FCSTD DOCUMENT  (FreeCAD 0.20R26155 (Git))
Label: SWD_pogo
License: All rights reserved
LicenseURL: http://en.wikipedia.org/wiki/All_rights_reserved
objects: Sketcher::SketchObject×2
note: 2 computed .brp shape members not serialized (recipe doc carries the construction recipe); baked Part::Feature solids carry a one-line shape summary decoded from their .brp

FEATURE [Sketcher::SketchObject] Sketch  label="Pads_TH_SMD"
  FullyConstrained = true
  sketch-geometry (15):
    g0: LineSegment StartX=-0.35 StartY=0 StartZ=0 EndX=0.35 EndY=0 EndZ=0
    g1: LineSegment StartX=0.35 StartY=0 StartZ=0 EndX=0.35 EndY=2.2 EndZ=0
    g2: LineSegment StartX=0.35 StartY=2.2 StartZ=0 EndX=-0.35 EndY=2.2 EndZ=0
    g3: LineSegment StartX=-0.35 StartY=2.2 StartZ=0 EndX=-0.35 EndY=0 EndZ=0
    g4: LineSegment StartX=1.85 StartY=-2.2e-15 StartZ=0 EndX=2.55 EndY=-2.2e-15 EndZ=0
    g5: LineSegment StartX=2.55 StartY=-2.2e-15 StartZ=0 EndX=2.55 EndY=2.2 EndZ=0
    g6: LineSegment StartX=2.55 StartY=2.2 StartZ=0 EndX=1.85 EndY=2.2 EndZ=0
    g7: LineSegment StartX=1.85 StartY=2.2 StartZ=0 EndX=1.85 EndY=-2.2e-15 EndZ=0
    g8: LineSegment StartX=-2.55 StartY=2.7e-15 StartZ=0 EndX=-1.85 EndY=2.7e-15 EndZ=0
    g9: LineSegment StartX=-1.85 StartY=2.7e-15 StartZ=0 EndX=-1.85 EndY=2.2 EndZ=0
    g10: LineSegment StartX=-1.85 StartY=2.2 StartZ=0 EndX=-2.55 EndY=2.2 EndZ=0
    g11: LineSegment StartX=-2.55 StartY=2.2 StartZ=0 EndX=-2.55 EndY=2.7e-15 EndZ=0
    g12: LineSegment StartX=-2.55 StartY=2.2 StartZ=0 EndX=2.55 EndY=2.2 EndZ=0
    g13: LineSegment StartX=-2.2 StartY=2.2 StartZ=0 EndX=-2.2 EndY=2.7e-15 EndZ=0
    g14: LineSegment StartX=2.2 StartY=2.2 StartZ=0 EndX=2.2 EndY=-2.2e-15 EndZ=0
  constraints (43):
    c: Coincident(g0,g1)
    c: Coincident(g1,g2)
    c: Coincident(g2,g3)
    c: Coincident(g3,g0)
    c: Horizontal(g0)
    c: Vertical(g1)
    c: Vertical(g3)
    c: Coincident(g4,g5)
    c: Coincident(g5,g6)
    c: Coincident(g6,g7)
    c: Coincident(g7,g4)
    c: Horizontal(g4)
    c: Horizontal(g6)
    c: Vertical(g5)
    c: Vertical(g7)
    c: Coincident(g8,g9)
    c: Coincident(g9,g10)
    c: Coincident(g10,g11)
    c: Coincident(g11,g8)
    c: Horizontal(g8)
    c: Horizontal(g10)
    c: Vertical(g9)
    c: Vertical(g11)
    c: Equal(g2,g6)
    c: Equal(g6,g10)
    c: Equal(g9,g1)
    c: Equal(g1,g5)
    c: Coincident(g12,g10)
    c: Coincident(g12,g5)
    c: Horizontal(g12)
    c: PointOnObject(g1,g12)
    c: DistanceY(g11,g11) = 2.2
    c: Symmetric(g2,g1,g-2)
    c: PointOnObject(g13,g10)
    c: PointOnObject(g13,g8)
    c: PointOnObject(g14,g6)
    c: PointOnObject(g14,g4)
    c: Symmetric(g6,g5,g14)
    c: Symmetric(g10,g9,g13)
    c: DistanceX(g13,g-1) = 2.2
    c: DistanceX(g-1,g14) = 2.2
    c: DistanceX(g8,g8) = 0.7
    c: PointOnObject(g0,g-1)
FEATURE [Sketcher::SketchObject] Sketch001  label="Edge_Cuts_0.15"
  ExternalGeometry = -> [Sketch]
  FullyConstrained = true
  sketch-geometry (21):
    g0: LineSegment StartX=-3.05 StartY=2.7 StartZ=0 EndX=3.05 EndY=2.7 EndZ=0
    g1: LineSegment StartX=3.55 StartY=3.2 StartZ=0 EndX=3.55 EndY=9.2 EndZ=0
    g2: LineSegment StartX=4.05 StartY=9.7 StartZ=0 EndX=6.05 EndY=9.7 EndZ=0
    g3: LineSegment StartX=7.5 StartY=-28.3 StartZ=0 EndX=-4.5 EndY=-28.3 EndZ=0
    g4: ArcOfCircle CenterX=4.05 CenterY=9.2 CenterZ=0 NormalX=0 NormalY=0 NormalZ=1 AngleXU=0 Radius=0.5 StartAngle=1.5708 EndAngle=3.14159
    g5: ArcOfCircle CenterX=6.05 CenterY=9.2 CenterZ=0 NormalX=0 NormalY=0 NormalZ=1 AngleXU=0 Radius=0.5 StartAngle=-9e-16 EndAngle=1.5708
    g6: ArcOfCircle CenterX=-3.05 CenterY=2.2 CenterZ=0 NormalX=0 NormalY=0 NormalZ=1 AngleXU=0 Radius=0.5 StartAngle=1.5708 EndAngle=3.14159
    g7: ArcOfCircle CenterX=3.05 CenterY=3.2 CenterZ=0 NormalX=0 NormalY=0 NormalZ=1 AngleXU=0 Radius=0.5 StartAngle=4.71239 EndAngle=6.28319
    g8: ArcOfCircle CenterX=-4.5 CenterY=-27.8 CenterZ=0 NormalX=0 NormalY=0 NormalZ=1 AngleXU=0 Radius=0.5 StartAngle=3.14159 EndAngle=4.71239
    g9: ArcOfCircle CenterX=7.5 CenterY=-27.8 CenterZ=0 NormalX=0 NormalY=0 NormalZ=1 AngleXU=0 Radius=0.5 StartAngle=4.71239 EndAngle=6.28319
    g10: LineSegment StartX=-5 StartY=-27.8 StartZ=0 EndX=-5 EndY=-16.8 EndZ=0
    g11: LineSegment StartX=-4.5 StartY=-16.3 StartZ=0 EndX=-4.05 EndY=-16.3 EndZ=0
    g12: LineSegment StartX=-3.55 StartY=-15.8 StartZ=0 EndX=-3.55 EndY=2.2 EndZ=0
    g13: LineSegment StartX=6.55 StartY=9.2 StartZ=0 EndX=6.55 EndY=-15.8 EndZ=0
    g14: LineSegment StartX=7.05 StartY=-16.3 StartZ=0 EndX=7.5 EndY=-16.3 EndZ=0
    g15: LineSegment StartX=8 StartY=-16.8 StartZ=0 EndX=8 EndY=-27.8 EndZ=0
    g16: ArcOfCircle CenterX=-4.5 CenterY=-16.8 CenterZ=0 NormalX=0 NormalY=0 NormalZ=1 AngleXU=0 Radius=0.5 StartAngle=1.5708 EndAngle=3.14159
    g17: ArcOfCircle CenterX=7.5 CenterY=-16.8 CenterZ=0 NormalX=0 NormalY=0 NormalZ=1 AngleXU=0 Radius=0.5 StartAngle=-2.7e-15 EndAngle=1.5708
    g18: ArcOfCircle CenterX=-4.05 CenterY=-15.8 CenterZ=0 NormalX=0 NormalY=0 NormalZ=1 AngleXU=0 Radius=0.5 StartAngle=4.71239 EndAngle=6.28319
    g19: ArcOfCircle CenterX=7.05 CenterY=-15.8 CenterZ=0 NormalX=0 NormalY=0 NormalZ=1 AngleXU=0 Radius=0.5 StartAngle=3.14159 EndAngle=4.71239
    g20: LineSegment StartX=-4.05 StartY=-16.3 StartZ=0 EndX=7.05 EndY=-16.3 EndZ=0
  constraints (53):
    c: Horizontal(g0)
    c: Vertical(g1)
    c: Horizontal(g2)
    c: Horizontal(g3)
    c: Tangent(g1,g4) = 1.5708
    c: Tangent(g2,g4) = 1.5708
    c: Tangent(g2,g5) = 1.5708
    c: Equal(g5,g4)
    c: Radius(g5) = 0.5
    c: Tangent(g0,g6) = 1.5708
    c: Tangent(g0,g7) = -1.5708
    c: Tangent(g1,g7) = -1.5708
    c: Equal(g7,g6)
    c: Equal(g6,g4)
    c: DistanceY(g-3,g0) = 0.5
    c: DistanceY(g0,g2) = 7
    c: DistanceX(g-4,g1) = 1
    c: Tangent(g3,g8) = 1.5708
    c: Tangent(g3,g9) = 1.5708
    c: Equal(g8,g9)
    c: Equal(g9,g6)
    c: DistanceY(g3,g2) = 38
    c: DistanceX(g3,g3) = 12
    c: Tangent(g8,g10) = 1.5708
    c: Horizontal(g11)
    c: Vertical(g12)
    c: Tangent(g5,g13) = 1.5708
    c: Horizontal(g14)
    c: Coincident(g15,g9)
    c: Vertical(g15)
    c: Tangent(g10,g16) = 1.5708
    c: Tangent(g11,g16) = 1.5708
    c: Tangent(g14,g17) = 1.5708
    c: Tangent(g15,g17) = 1.5708
    c: Tangent(g11,g18) = -1.5708
    c: Tangent(g12,g18) = -1.5708
    c: Tangent(g13,g19) = -1.5708
    c: Tangent(g14,g19) = -1.5708
    c: Equal(g11,g14)
    c: Equal(g16,g18)
    c: Equal(g18,g19)
    c: Equal(g19,g17)
    c: Equal(g17,g9)
    c: Equal(g10,g15)
    c: Coincident(g20,g11)
    c: Coincident(g20,g14)
    c: Horizontal(g20)
    c: Vertical(g13)
    c: DistanceY(g3,g11) = 12
    c: Vertical(g10)
    c: DistanceX(g6,g-3) = 1
    c: DistanceX(g1,g5) = 3
    c: Tangent(g12,g6) = 1.5708
